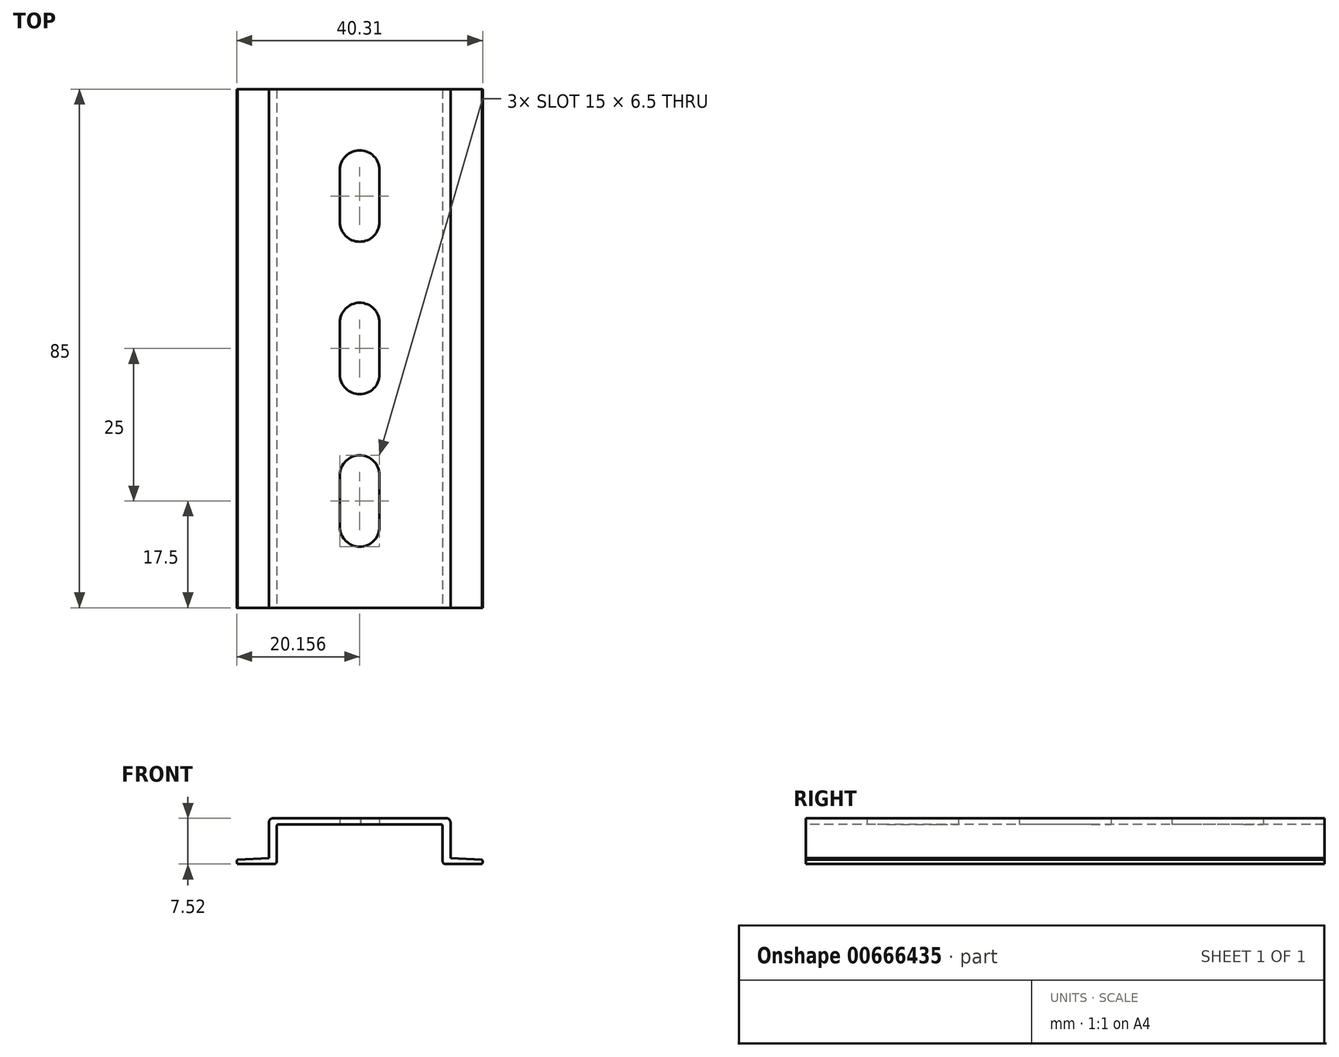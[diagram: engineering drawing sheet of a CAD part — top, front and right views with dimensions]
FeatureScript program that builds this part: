
annotation { "Feature Type Name" : "Feature", "Feature Type Description" : "" }
export const myFeature = defineFeature(function(context is Context, id is Id, definition is map)
    precondition{}
    {
        {
            var Q0;
            Q0=qCreatedBy(makeId("Front.planeOp"),FACE);
            var sketch = newSketch(context, id + "F0", { "sketchPlane" : qUnion([Q0])});
            skLineSegment(sketch, "E0.0", {"start": v(0, 1.23) * mm, "end": v(5.15, 1.49) * mm});
            skFitSpline(sketch, "E1.0.0", {"points": [v(40.07, 0.49) * mm, v(40.2, 0.86) * mm, v(40.07, 1.23) * mm]});
            skLineSegment(sketch, "E1.0.1", {"start": v(40.07, 1.23) * mm, "end": v(34.92, 1.49) * mm});
            skLineSegment(sketch, "E1.0.2", {"start": v(34.92, 1.49) * mm, "end": v(34.92, 7.31) * mm});
            skArc(sketch, "E1.0.3", {"start": v(34.92, 7.31) * mm, "mid": v(34.71, 7.8) * mm, "end": v(34.22, 8.01) * mm});
            skLineSegment(sketch, "E1.0.4", {"start": v(34.22, 8.01) * mm, "end": v(5.85, 8.01) * mm});
            skArc(sketch, "E1.0.5", {"start": v(5.85, 8.01) * mm, "mid": v(5.36, 7.8) * mm, "end": v(5.15, 7.31) * mm});
            skLineSegment(sketch, "E1.0.6", {"start": v(5.15, 7.31) * mm, "end": v(5.15, 1.49) * mm});
            skLineSegment(sketch, "E1.0.7", {"start": v(5.15, 1.49) * mm, "end": v(0, 1.23) * mm});
            skFitSpline(sketch, "E1.0.8", {"points": [v(0, 1.23) * mm, v(-0.12, 0.86) * mm, v(0, 0.49) * mm]});
            skLineSegment(sketch, "E1.0.9", {"start": v(0, 0.49) * mm, "end": v(5.95, 0.49) * mm});
            skArc(sketch, "E1.0.10", {"start": v(5.95, 0.49) * mm, "mid": v(6.3, 0.63) * mm, "end": v(6.45, 0.99) * mm});
            skLineSegment(sketch, "E1.0.11", {"start": v(6.45, 0.99) * mm, "end": v(6.45, 6.71) * mm});
            skArc(sketch, "E1.0.12", {"start": v(6.45, 6.71) * mm, "mid": v(6.54, 6.93) * mm, "end": v(6.75, 7.01) * mm});
            skLineSegment(sketch, "E1.0.13", {"start": v(6.75, 7.01) * mm, "end": v(33.32, 7.01) * mm});
            skArc(sketch, "E1.0.14", {"start": v(33.32, 7.01) * mm, "mid": v(33.53, 6.93) * mm, "end": v(33.62, 6.71) * mm});
            skLineSegment(sketch, "E1.0.15", {"start": v(33.62, 6.71) * mm, "end": v(33.62, 0.99) * mm});
            skArc(sketch, "E1.0.16", {"start": v(33.62, 0.99) * mm, "mid": v(33.77, 0.63) * mm, "end": v(34.12, 0.49) * mm});
            skLineSegment(sketch, "E1.0.17", {"start": v(34.12, 0.49) * mm, "end": v(40.07, 0.49) * mm});
            skSolve(sketch);
        }
        {
            var Q0;
            Q0=qSketchRegion(id+"F0",true);
            extrude(context, id + "F1", {"entities" : qUnion([Q0]), "oppositeDirection" : true, "depth" : 85 * mm, "offsetDistance" : 25 * mm});
        }
        {
            var Q0;
            Q0=qCreatedBy(makeId("Top.planeOp"),FACE);
            var sketch = newSketch(context, id + "F2", { "sketchPlane" : qUnion([Q0])});
            skLineSegment(sketch, "E2.0", {"start": v(16.79, 21.75) * mm, "end": v(16.79, 13.25) * mm});
            skArc(sketch, "E3.0", {"start": v(23.29, 21.75) * mm, "mid": v(20.04, 25) * mm, "end": v(16.79, 21.75) * mm});
            skLineSegment(sketch, "E4.0", {"start": v(23.29, 13.25) * mm, "end": v(23.29, 21.75) * mm});
            skArc(sketch, "E5.0", {"start": v(16.79, 13.25) * mm, "mid": v(20.04, 10) * mm, "end": v(23.29, 13.25) * mm});
            skArc(sketch, "E6.0", {"start": v(16.79, 38.25) * mm, "mid": v(20.04, 35) * mm, "end": v(23.29, 38.25) * mm});
            skArc(sketch, "E7.0", {"start": v(23.29, 46.75) * mm, "mid": v(20.04, 50) * mm, "end": v(16.79, 46.75) * mm});
            skLineSegment(sketch, "E8.0", {"start": v(23.29, 38.25) * mm, "end": v(23.29, 46.75) * mm});
            skLineSegment(sketch, "E9.0", {"start": v(23.29, 63.25) * mm, "end": v(23.29, 71.75) * mm});
            skArc(sketch, "E10.0", {"start": v(23.29, 71.75) * mm, "mid": v(20.04, 75) * mm, "end": v(16.79, 71.75) * mm});
            skLineSegment(sketch, "E11.0", {"start": v(16.79, 71.75) * mm, "end": v(16.79, 63.25) * mm});
            skArc(sketch, "E12.0", {"start": v(16.79, 63.25) * mm, "mid": v(20.04, 60) * mm, "end": v(23.29, 63.25) * mm});
            skLineSegment(sketch, "E13", {"start": v(16.79, 46.75) * mm, "end": v(16.79, 38.25) * mm});
            skLineSegment(sketch, "E14.1.0.0", {"start": v(23.43, 88.25) * mm, "end": v(23.43, 96.75) * mm});
            skArc(sketch, "E14.1.0.1", {"start": v(16.93, 88.25) * mm, "mid": v(20.18, 85) * mm, "end": v(23.43, 88.25) * mm});
            skLineSegment(sketch, "E14.1.0.2", {"start": v(16.93, 96.75) * mm, "end": v(16.93, 88.25) * mm});
            skArc(sketch, "E14.1.0.3", {"start": v(23.43, 96.75) * mm, "mid": v(20.18, 100) * mm, "end": v(16.93, 96.75) * mm});
            skLineSegment(sketch, "E14.2.0.0", {"start": v(23.57, 113.25) * mm, "end": v(23.57, 121.75) * mm});
            skArc(sketch, "E14.2.0.1", {"start": v(17.07, 113.25) * mm, "mid": v(20.32, 110) * mm, "end": v(23.57, 113.25) * mm});
            skLineSegment(sketch, "E14.2.0.2", {"start": v(17.07, 121.75) * mm, "end": v(17.07, 113.25) * mm});
            skArc(sketch, "E14.2.0.3", {"start": v(23.57, 121.75) * mm, "mid": v(20.32, 125) * mm, "end": v(17.07, 121.75) * mm});
            skLineSegment(sketch, "E14.3.0.0", {"start": v(23.7, 138.25) * mm, "end": v(23.7, 146.75) * mm});
            skArc(sketch, "E14.3.0.1", {"start": v(17.2, 138.25) * mm, "mid": v(20.46, 135) * mm, "end": v(23.7, 138.25) * mm});
            skLineSegment(sketch, "E14.3.0.2", {"start": v(17.2, 146.75) * mm, "end": v(17.2, 138.25) * mm});
            skArc(sketch, "E14.3.0.3", {"start": v(23.7, 146.75) * mm, "mid": v(20.46, 150) * mm, "end": v(17.2, 146.75) * mm});
            skLineSegment(sketch, "E14.4.0.0", {"start": v(23.85, 163.25) * mm, "end": v(23.85, 171.75) * mm});
            skArc(sketch, "E14.4.0.1", {"start": v(17.35, 163.25) * mm, "mid": v(20.6, 160) * mm, "end": v(23.85, 163.25) * mm});
            skLineSegment(sketch, "E14.4.0.2", {"start": v(17.35, 171.75) * mm, "end": v(17.35, 163.25) * mm});
            skArc(sketch, "E14.4.0.3", {"start": v(23.85, 171.75) * mm, "mid": v(20.6, 175) * mm, "end": v(17.35, 171.75) * mm});
            skLineSegment(sketch, "E14.5.0.0", {"start": v(24, 188.25) * mm, "end": v(24, 196.75) * mm});
            skArc(sketch, "E14.5.0.1", {"start": v(17.5, 188.25) * mm, "mid": v(20.74, 185) * mm, "end": v(24, 188.25) * mm});
            skLineSegment(sketch, "E14.5.0.2", {"start": v(17.5, 196.75) * mm, "end": v(17.5, 188.25) * mm});
            skArc(sketch, "E14.5.0.3", {"start": v(24, 196.75) * mm, "mid": v(20.74, 200) * mm, "end": v(17.5, 196.75) * mm});
            skLineSegment(sketch, "E14.direction1", {"start": v(16.79, 63.25) * mm, "end": v(16.93, 88.25) * mm, "construction": true});
            skSolve(sketch);
        }
        {
            var Q0;
            Q0=qSketchRegion(id+"F2",true);
            extrude(context, id + "F3", {"entities" : qUnion([Q0]), "operationType" : NewBodyOperationType.REMOVE, "endBound" : BoundingType.THROUGH_ALL, "depth" : 25 * mm, "offsetDistance" : 25 * mm});
        }
    });
